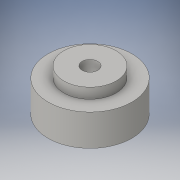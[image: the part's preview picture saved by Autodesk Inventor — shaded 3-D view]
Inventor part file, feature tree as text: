
AUTODESK INVENTOR PART (.ipt)
format: ipt  version: 2016 (Build 200138000, 138)  size: 109,568 bytes
history: native  units: in
note: dims shown in document units (in); Inventor stores cm internally (conversion verified against a paired STEP export)
features: extrude x4, sketch x4
ambient origin geometry x8: Origin, YZ Plane, XZ Plane, XY Plane, X Axis, Y Axis, Z Axis, Center Point
bodies: Solid1 (feature_tree)
feature tree (8):
  extrude  "Extrusion1"  Depth=0.75in TaperAngle=0.0deg
  extrude  "Extrusion2"  Depth=0.25in TaperAngle=0.0deg
  extrude  "Extrusion3"  Depth=1.25in TaperAngle=0.0deg
  extrude  "Extrusion4"  Depth=1.25in TaperAngle=0.0deg
  sketch  "Sketch1"  dims[d0=2.0in d1=0.75in d2=0.0in]
  sketch  "Sketch2"  dims[d3=1.25in d4=0.25in d5=0.0in]
  sketch  "Sketch3"  dims[d6=0.375in d7=1.25in d8=0.0in]
  sketch  "Sketch4"  dims[d9=0.375in d10=1.25in d11=0.0in]
